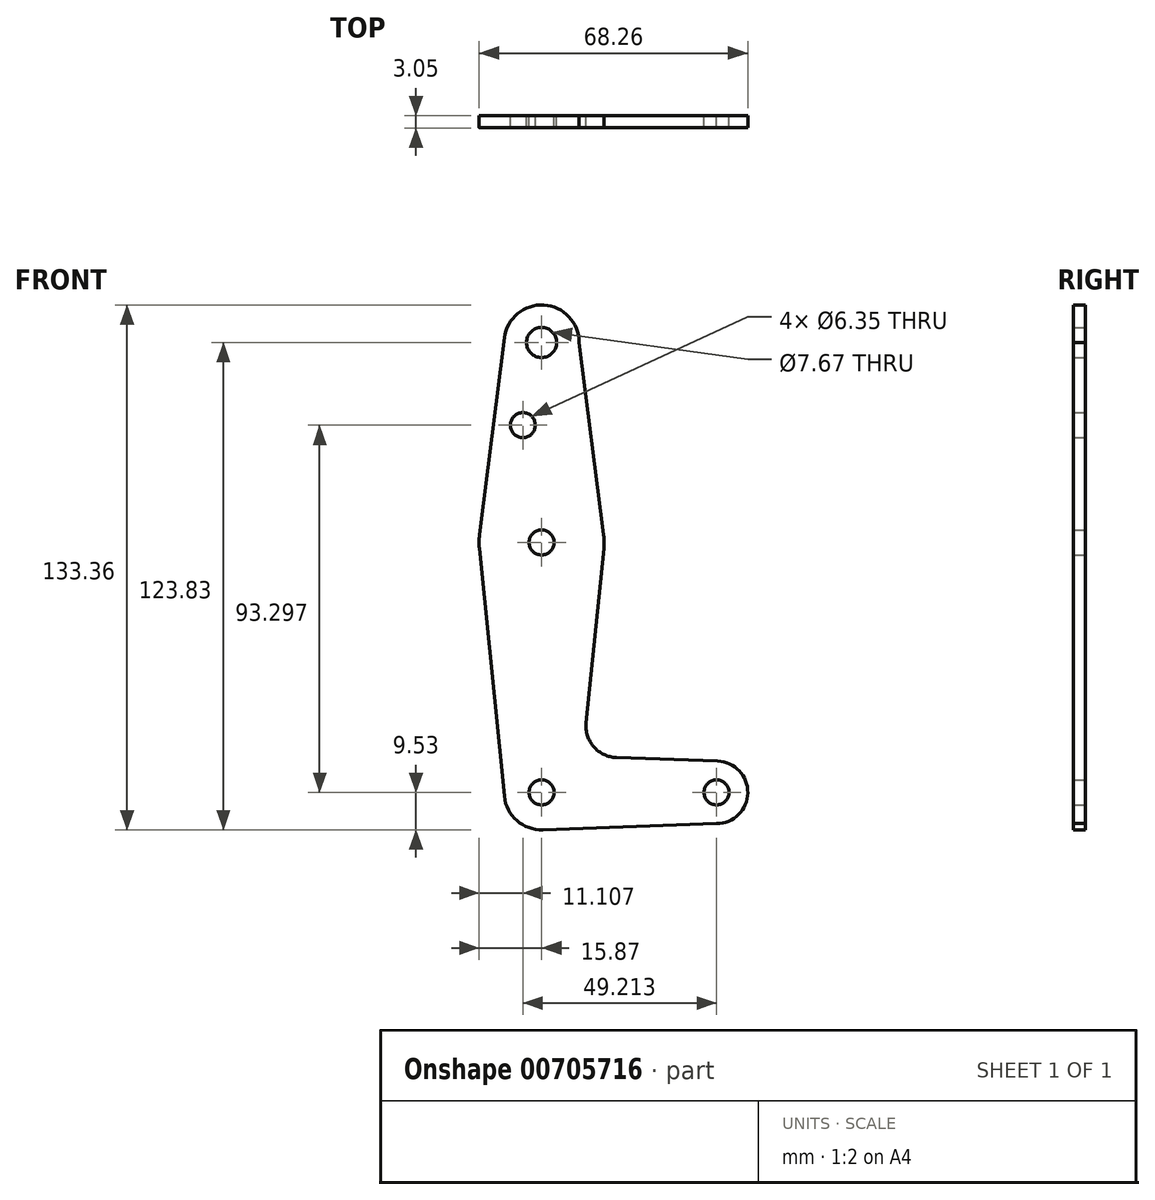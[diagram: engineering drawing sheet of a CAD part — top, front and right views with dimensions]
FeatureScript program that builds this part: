
annotation { "Feature Type Name" : "Feature", "Feature Type Description" : "" }
export const myFeature = defineFeature(function(context is Context, id is Id, definition is map)
    precondition{}
    {
        {
            var Q0;
            Q0=qCreatedBy(makeId("Front.planeOp"),FACE);
            var sketch = newSketch(context, id + "F0", { "sketchPlane" : qUnion([Q0])});
            skLineSegment(sketch, "E0", {"start": v(0, 0) * mm, "end": v(0, 49.32) * mm, "construction": true});
            skLineSegment(sketch, "E1", {"start": v(0, 49.32) * mm, "end": v(0, 114.3) * mm, "construction": true});
            skLineSegment(sketch, "E2", {"start": v(0, 0) * mm, "end": v(44.45, 0) * mm, "construction": true});
            skCircle(sketch, "E3", {"center": v(0, 0) * mm, "radius": 9.53 * mm});
            skCircle(sketch, "E4", {"center": v(44.45, 0) * mm, "radius": 7.94 * mm});
            skCircle(sketch, "E5", {"center": v(0, 114.3) * mm, "radius": 9.53 * mm});
            skCircle(sketch, "E6", {"center": v(0, 63.5) * mm, "radius": 15.88 * mm});
            skLineSegment(sketch, "E7", {"start": v(-9.45, 115.5) * mm, "end": v(-15.75, 65.48) * mm});
            skLineSegment(sketch, "E8", {"start": v(9.53, 114.3) * mm, "end": v(15.75, 65.5) * mm});
            skLineSegment(sketch, "E9", {"start": v(18.97, 8.85) * mm, "end": v(44.73, 7.93) * mm});
            skLineSegment(sketch, "E10", {"start": v(44.45, -7.94) * mm, "end": v(0, -9.53) * mm});
            skLineSegment(sketch, "E11", {"start": v(-15.8, 61.91) * mm, "end": v(-9.48, -0.95) * mm});
            skLineSegment(sketch, "E12", {"start": v(15.8, 61.91) * mm, "end": v(11.34, 17.59) * mm});
            skCircle(sketch, "E13", {"center": v(0, 114.3) * mm, "radius": 3.84 * mm});
            skCircle(sketch, "E14", {"center": v(0, 63.5) * mm, "radius": 3.18 * mm});
            skCircle(sketch, "E15", {"center": v(0, 0) * mm, "radius": 3.18 * mm});
            skCircle(sketch, "E16", {"center": v(44.45, 0) * mm, "radius": 3.18 * mm});
            skCircle(sketch, "E17", {"center": v(-4.76, 93.3) * mm, "radius": 3.18 * mm});
            skPoint(sketch, "E18.newPointA", {"position": v(9.48, -0.95) * mm});
            skPoint(sketch, "E18.newPointB", {"position": v(0, 9.53) * mm});
            skArc(sketch, "E18.filletArc", {"start": v(11.34, 17.59) * mm, "mid": v(13.26, 11.57) * mm, "end": v(18.97, 8.85) * mm});
            skSolve(sketch);
        }
        {
            var Q0;
            Q0 = qSketchRegion(id + "F0", true);
            extrude(context, id + "F1", {"entities" : qUnion([Q0]), "depth" : 3.05 * mm, "offsetDistance" : 25.4 * mm});
        }
    });
